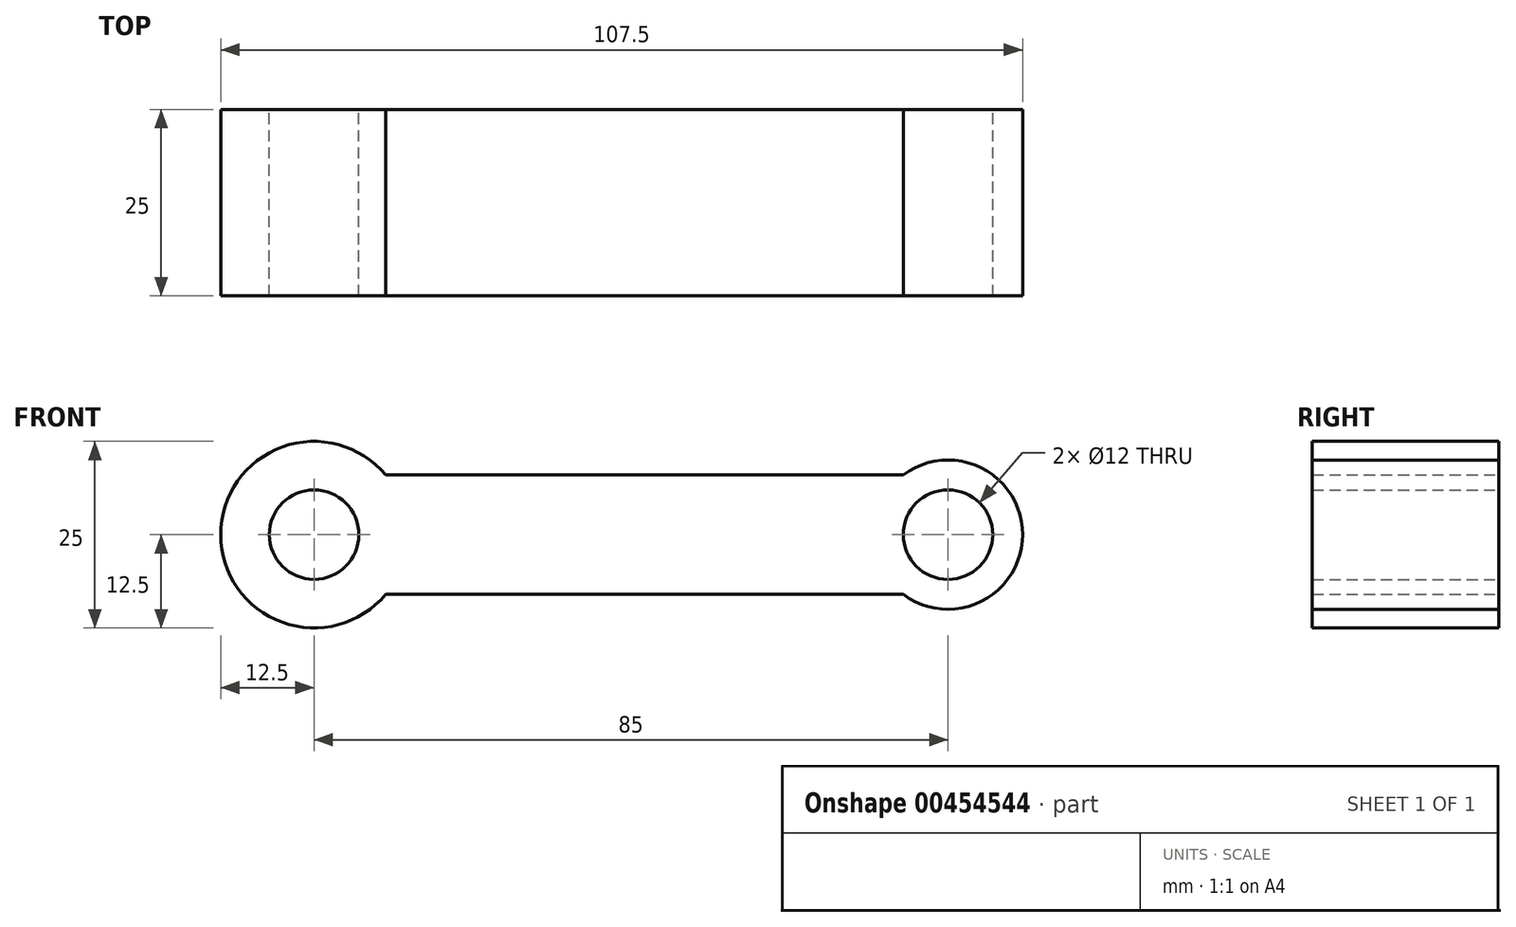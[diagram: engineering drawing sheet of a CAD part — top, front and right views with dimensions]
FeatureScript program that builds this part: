
annotation { "Feature Type Name" : "Feature", "Feature Type Description" : "" }
export const myFeature = defineFeature(function(context is Context, id is Id, definition is map)
    precondition{}
    {
        {
            var Q0;
            Q0=qCreatedBy(makeId("Front.planeOp"),FACE);
            var sketch = newSketch(context, id + "F0", { "sketchPlane" : qUnion([Q0])});
            skCircle(sketch, "E0", {"center": v(0, 0) * mm, "radius": 12.5 * mm});
            skCircle(sketch, "E1", {"center": v(85, 0) * mm, "radius": 10 * mm});
            skLineSegment(sketch, "E2", {"start": v(0, 0) * mm, "end": v(85, 0) * mm, "construction": true});
            skCircle(sketch, "E3", {"center": v(0, 0) * mm, "radius": 6 * mm});
            skCircle(sketch, "E4", {"center": v(85, 0) * mm, "radius": 6 * mm});
            skLineSegment(sketch, "E5", {"start": v(9.6, 8) * mm, "end": v(79, 8) * mm});
            skLineSegment(sketch, "E6.MirrorCS", {"start": v(9.6, -8) * mm, "end": v(79, -8) * mm});
            skSolve(sketch);
        }
        {
            var Q0;
            Q0 = qSketchRegion(id + "F0", true);
            extrude(context, id + "F1", {"entities" : qUnion([Q0]), "depth" : 25 * mm});
        }
    });
